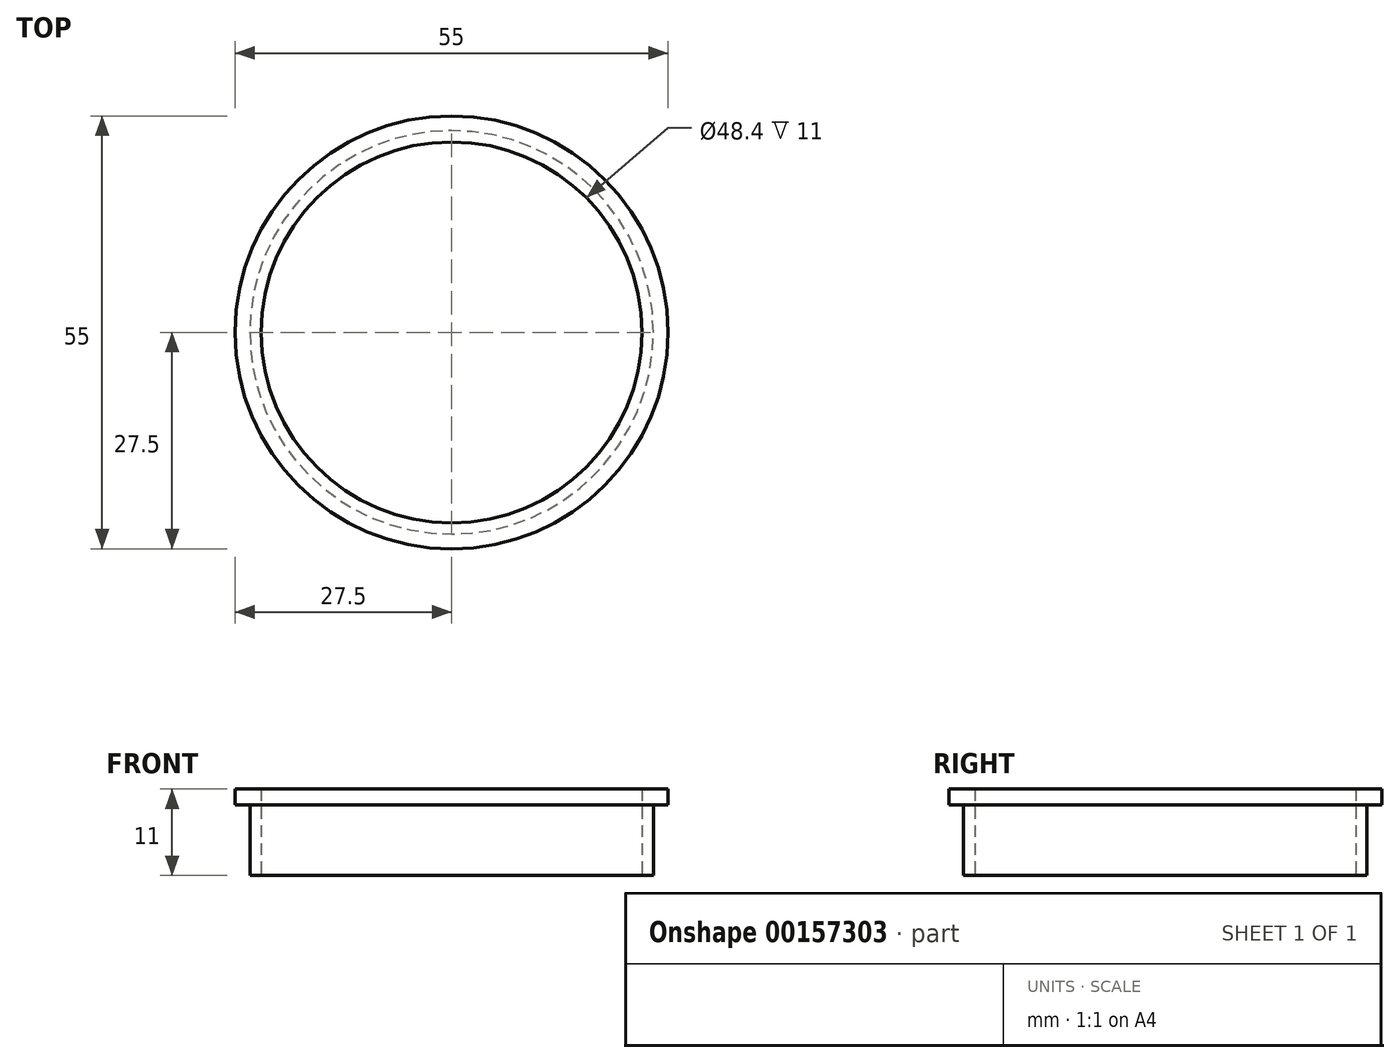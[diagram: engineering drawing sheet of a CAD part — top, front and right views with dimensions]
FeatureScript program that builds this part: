
annotation { "Feature Type Name" : "Feature", "Feature Type Description" : "" }
export const myFeature = defineFeature(function(context is Context, id is Id, definition is map)
    precondition{}
    {
        {
            var Q0;
            Q0=qCreatedBy(makeId("Top.planeOp"),FACE);
            var sketch = newSketch(context, id + "F0", { "sketchPlane" : qUnion([Q0])});
            skCircle(sketch, "E0", {"center": v(0, 0) * mm, "radius": 24.2 * mm});
            skCircle(sketch, "E1", {"center": v(0, 0) * mm, "radius": 25.63 * mm});
            skSolve(sketch);
        }
        {
            var Q0;
            Q0=makeQuery(id+"F0.imprint","IMPRINT",FACE,{"disambiguationData":[TD([[makeQuery(id+"F0.imprint","IMPRINT",EDGE,{"derivedFrom":sQuery(id+"F0.wireOp",EDGE,"E0")}),-1.0]])]});
            extrude(context, id + "F1", {"entities" : qUnion([Q0]), "depth" : 9 * mm});
        }
        {
            var Q0;
            Q0=makeQuery(id+"F1.opExtrude","CAP_FACE",FACE,{"disambiguationData":[OSD([sQuery(id+"F0.wireOp",EDGE,"E0"),sQuery(id+"F0.wireOp",EDGE,"E1")])],"isStart":false});
            var sketch = newSketch(context, id + "F2", { "sketchPlane" : qUnion([Q0])});
            skCircle(sketch, "E2", {"center": v(0, 0) * mm, "radius": 24 * mm});
            skCircle(sketch, "E3", {"center": v(0, 0) * mm, "radius": 27.5 * mm});
            skSolve(sketch);
        }
        {
            var Q0;
            Q0=makeQuery(id+"F2.imprint","IMPRINT",FACE,{"disambiguationData":[TD([[makeQuery(id+"F2.imprint","IMPRINT",EDGE,{"derivedFrom":makeQuery(id+"F1.opExtrude","CAP_EDGE",EDGE,{"disambiguationData":[OSD([sQuery(id+"F0.wireOp",EDGE,"E0")])],"isStart":false})}),-1.0]])]});
            var Q1;
            Q1=makeQuery(id+"F2.imprint","IMPRINT",FACE,{"disambiguationData":[TD([[makeQuery(id+"F2.imprint","IMPRINT",EDGE,{"derivedFrom":sQuery(id+"F2.wireOp",EDGE,"E3")}),1.0]])]});
            extrude(context, id + "F3", {"entities" : qUnion([Q0, Q1]), "operationType" : NewBodyOperationType.ADD, "depth" : 2 * mm});
        }
    });
